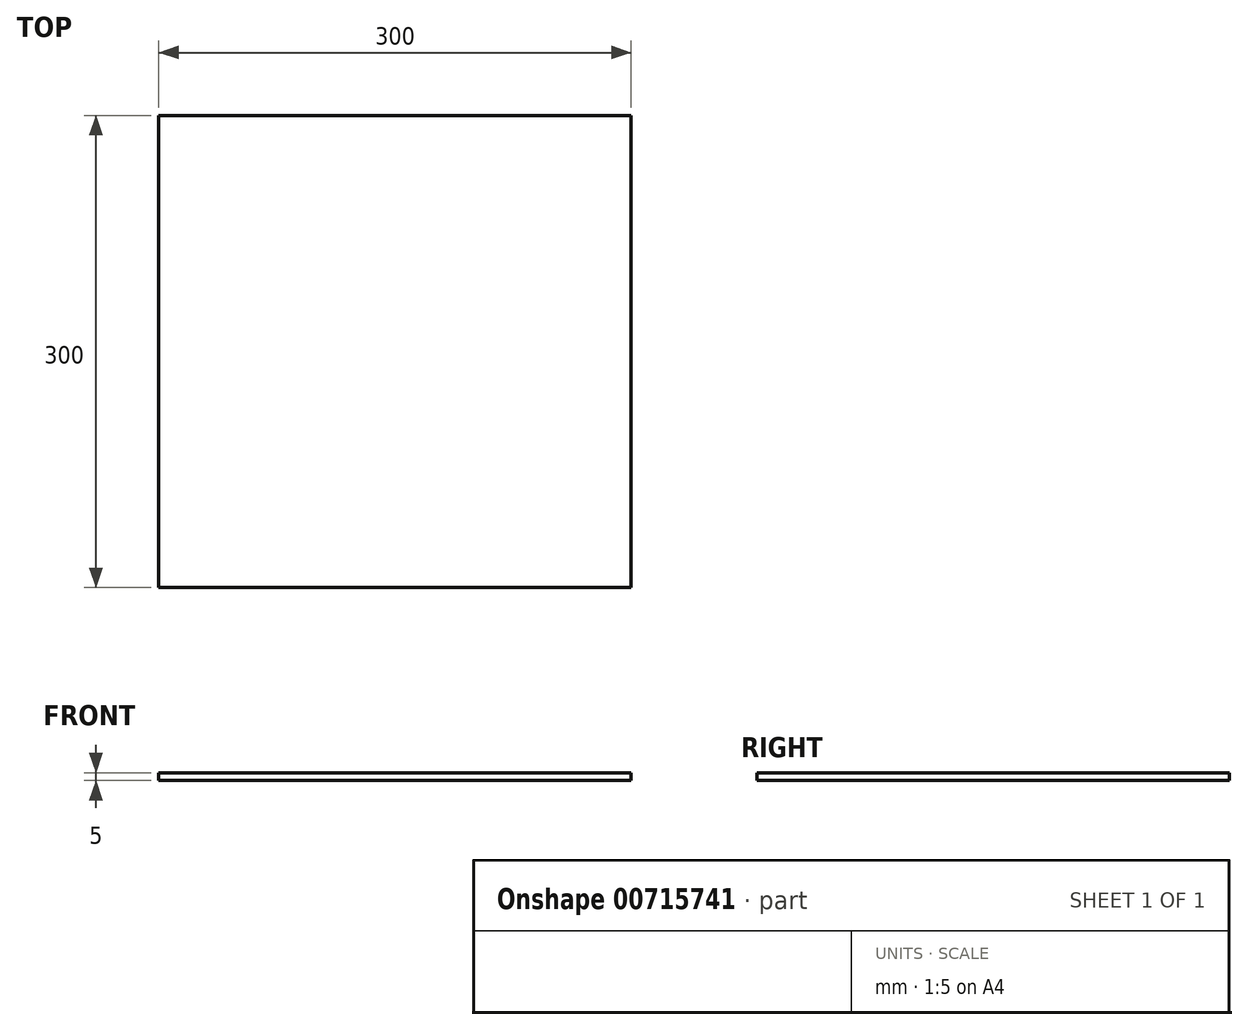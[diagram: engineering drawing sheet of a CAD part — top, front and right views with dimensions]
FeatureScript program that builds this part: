
annotation { "Feature Type Name" : "Feature", "Feature Type Description" : "" }
export const myFeature = defineFeature(function(context is Context, id is Id, definition is map)
    precondition{}
    {
        {
            var Q0;
            Q0=qCreatedBy(makeId("Top.planeOp"),FACE);
            var sketch = newSketch(context, id + "F0", { "sketchPlane" : qUnion([Q0])});
            skLineSegment(sketch, "E0.bottom", {"start": v(-150, 150) * mm, "end": v(150, 150) * mm});
            skLineSegment(sketch, "E0.top", {"start": v(-150, -150) * mm, "end": v(150, -150) * mm});
            skLineSegment(sketch, "E0.left", {"start": v(-150, 150) * mm, "end": v(-150, -150) * mm});
            skLineSegment(sketch, "E0.right", {"start": v(150, 150) * mm, "end": v(150, -150) * mm});
            skSolve(sketch);
        }
        {
            var Q0;
            Q0 = qSketchRegion(id + "F0", true);
            extrude(context, id + "F1", {"entities" : qUnion([Q0]), "depth" : 5 * mm, "offsetDistance" : 25 * mm});
        }
    });
